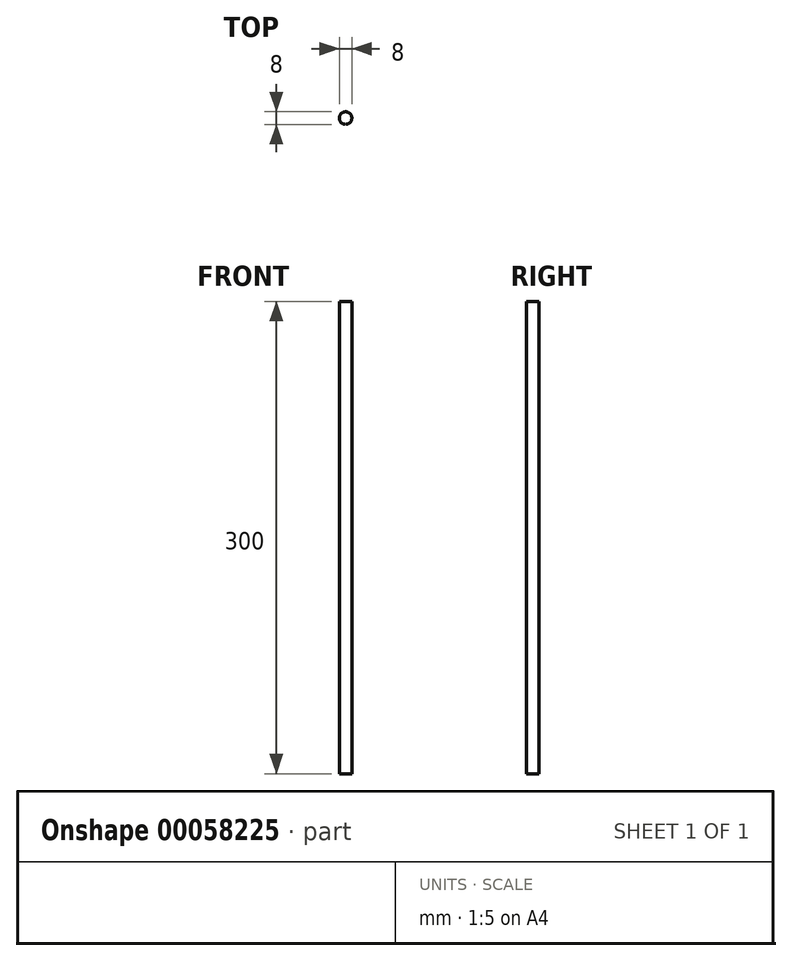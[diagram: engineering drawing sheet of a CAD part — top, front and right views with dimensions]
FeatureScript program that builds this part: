
annotation { "Feature Type Name" : "Feature", "Feature Type Description" : "" }
export const myFeature = defineFeature(function(context is Context, id is Id, definition is map)
    precondition{}
    {
        {
            var Q0;
            Q0=qCreatedBy(makeId("Top.planeOp"),FACE);
            var sketch = newSketch(context, id + "F0", { "sketchPlane" : qUnion([Q0])});
            skCircle(sketch, "E0", {"center": v(0, 0) * mm, "radius": 4 * mm});
            skSolve(sketch);
        }
        {
            var Q0;
            Q0=qSketchRegion(id+"F0",true);
            extrude(context, id + "F1", {"entities" : qUnion([Q0]), "depth" : 300 * mm});
        }
    });
